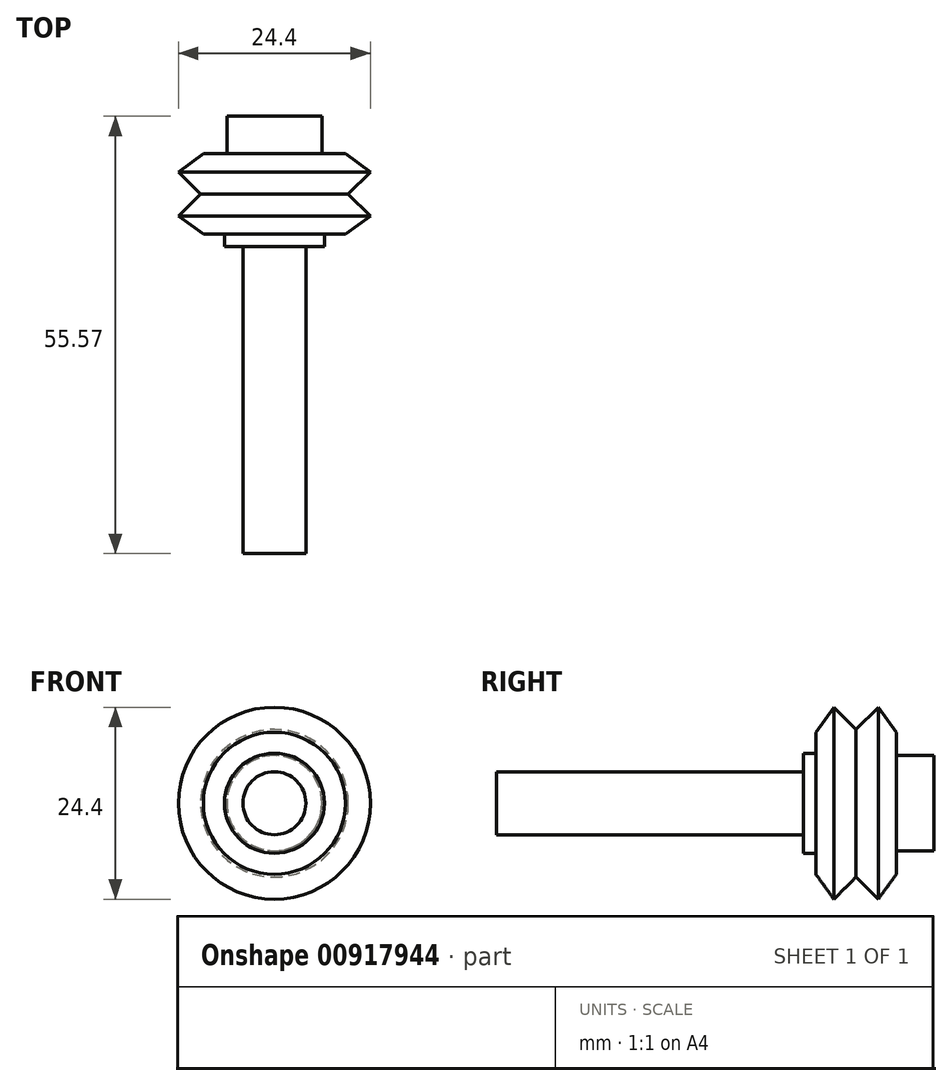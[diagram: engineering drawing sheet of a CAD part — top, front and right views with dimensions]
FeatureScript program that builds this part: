
annotation { "Feature Type Name" : "Feature", "Feature Type Description" : "" }
export const myFeature = defineFeature(function(context is Context, id is Id, definition is map)
    precondition{}
    {
        {
            var Q0;
            Q0=qCreatedBy(makeId("Right.planeOp"),FACE);
            var sketch = newSketch(context, id + "F0", { "sketchPlane" : qUnion([Q0])});
            skLineSegment(sketch, "E0", {"start": v(-5.11, 4) * mm, "end": v(5.12, 4) * mm});
            skLineSegment(sketch, "E1", {"start": v(5.11, 4) * mm, "end": v(5.11, 9.02) * mm});
            skLineSegment(sketch, "E2", {"start": v(5.11, 9.02) * mm, "end": v(2.81, 12.2) * mm});
            skLineSegment(sketch, "E3", {"start": v(2.81, 12.2) * mm, "end": v(0, 9.38) * mm});
            skLineSegment(sketch, "E4", {"start": v(0, 9.38) * mm, "end": v(-2.82, 12.2) * mm});
            skLineSegment(sketch, "E5", {"start": v(-2.81, 12.2) * mm, "end": v(-5.11, 9.02) * mm});
            skLineSegment(sketch, "E6", {"start": v(-5.11, 9.02) * mm, "end": v(-5.11, 4) * mm});
            skLineSegment(sketch, "E7", {"start": v(0, 9.38) * mm, "end": v(0, 4) * mm, "construction": true});
            skLineSegment(sketch, "E8", {"start": v(-25.32, 0) * mm, "end": v(23.47, 0) * mm, "construction": true});
            skLineSegment(sketch, "E9", {"start": v(-1.59, 10.97) * mm, "end": v(1.59, 10.97) * mm, "construction": true});
            skLineSegment(sketch, "E10", {"start": v(0, 10.97) * mm, "end": v(0, 0) * mm, "construction": true});
            skSolve(sketch);
        }
        {
            var Q0;
            Q0 = qSketchRegion(id + "F0", true);
            var Q1;
            Q1=sQuery(id+"F0.wireOp",EDGE,"E8");
            revolve(context, id + "F1", {"surfaceOperationType" : NewSurfaceOperationType.NEW, "entities" : qUnion([Q0]), "axis" : qUnion([Q1]), "revolveType" : RevolveType.FULL});
        }
        {
            var Q0;
            Q0=makeQuery(id+"F1.opRevolve","SWEPT_FACE",FACE,{"disambiguationData":[OSD([sQuery(id+"F0.wireOp",EDGE,"E6")])]});
            var sketch = newSketch(context, id + "F2", { "sketchPlane" : qUnion([Q0])});
            skCircle(sketch, "E11", {"center": v(0, 0) * mm, "radius": 6.35 * mm});
            skCircle(sketch, "E12.0", {"center": v(0, 0) * mm, "radius": 4 * mm});
            skSolve(sketch);
        }
        {
            var Q0;
            Q0 = qSketchRegion(id + "F2", true);
            extrude(context, id + "F3", {"entities" : qUnion([Q0]), "depth" : 1.59 * mm, "offsetDistance" : 25.4 * mm});
        }
        {
            var Q0;
            Q0=makeQuery(id+"F1.opRevolve","SWEPT_FACE",FACE,{"disambiguationData":[OSD([sQuery(id+"F0.wireOp",EDGE,"E1")])]});
            var sketch = newSketch(context, id + "F4", { "sketchPlane" : qUnion([Q0])});
            skCircle(sketch, "E13", {"center": v(0, 0) * mm, "radius": 6.04 * mm});
            skSolve(sketch);
        }
        {
            var Q0;
            Q0 = qSketchRegion(id + "F4", true);
            extrude(context, id + "F5", {"entities" : qUnion([Q0]), "depth" : 4.76 * mm, "offsetDistance" : 25.4 * mm});
        }
        {
            var Q0;
            Q0=makeQuery(id+"F5.opExtrude","CAP_FACE",FACE,{"disambiguationData":[OSD([sQuery(id+"F4.wireOp",EDGE,"E13")])],"isStart":true});
            var sketch = newSketch(context, id + "F6", { "sketchPlane" : qUnion([Q0])});
            skCircle(sketch, "E14.0", {"center": v(0, 0) * mm, "radius": 4 * mm});
            skSolve(sketch);
        }
        {
            var Q0;
            Q0 = qSketchRegion(id + "F6", true);
            extrude(context, id + "F7", {"entities" : qUnion([Q0]), "operationType" : NewBodyOperationType.ADD, "depth" : 50.8 * mm, "offsetDistance" : 25.4 * mm});
        }
    });
